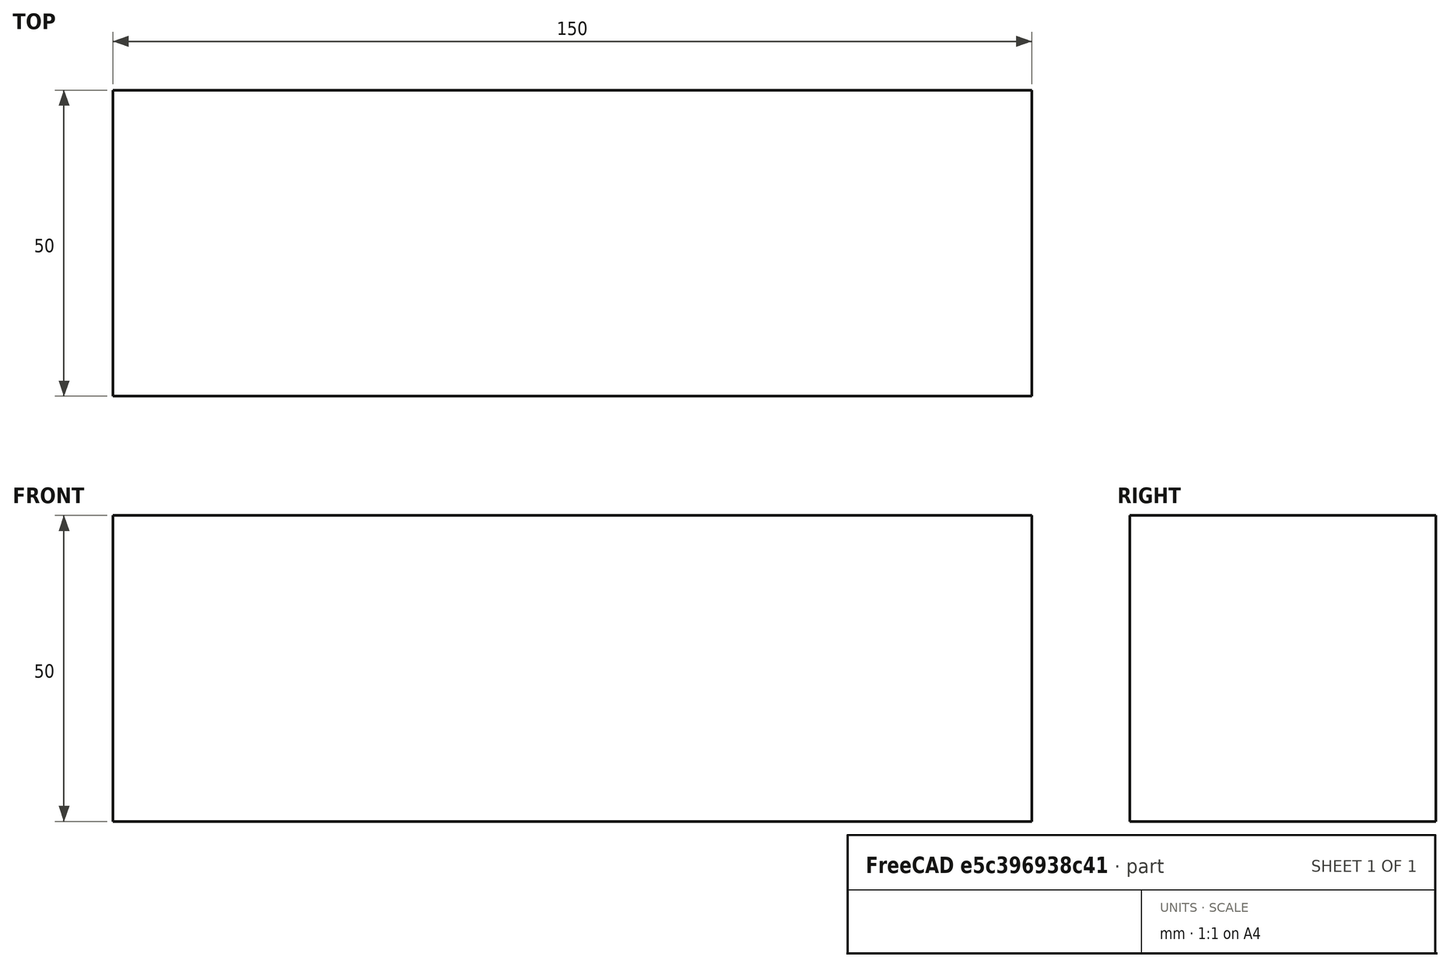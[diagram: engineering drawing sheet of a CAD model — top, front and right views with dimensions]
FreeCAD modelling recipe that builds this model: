
FCSTD DOCUMENT  (FreeCAD 0.15R4671 (Git))
Label: Flat Bar 150x50 EN10058 S235JR
License: All rights reserved
LicenseURL: http://en.wikipedia.org/wiki/All_rights_reserved
objects: Sketcher::SketchObject×1, Part::Extrusion×1
note: 2 computed .brp shape members not serialized (recipe doc carries the construction recipe); baked Part::Feature solids carry a one-line shape summary decoded from their .brp

FEATURE [Sketcher::SketchObject] Sketch
  sketch-geometry (4):
    g0: LineSegment StartX=-75 StartY=-25 StartZ=0 EndX=75 EndY=-25 EndZ=0
    g1: LineSegment StartX=75 StartY=-25 StartZ=0 EndX=75 EndY=25 EndZ=0
    g2: LineSegment StartX=75 StartY=25 StartZ=0 EndX=-75 EndY=25 EndZ=0
    g3: LineSegment StartX=-75 StartY=25 StartZ=0 EndX=-75 EndY=-25 EndZ=0
  constraints (12):
    c: Coincident(g0,g1)
    c: Coincident(g1,g2)
    c: Coincident(g2,g3)
    c: Coincident(g3,g0)
    c: Horizontal(g0)
    c: Horizontal(g2)
    c: Vertical(g1)
    c: Vertical(g3)
    c: Symmetric(g1,g2,g-2)
    c: Symmetric(g0,g1,g-1)
    c: DistanceY(g1) = 50
    c: DistanceX(g0) = 150
FEATURE [Part::Extrusion] Extrude  label="Flat Bar 150x50 EN10058 S235JR"
  Base = -> Sketch
  Dir = (0,0,50)
  Solid = true
